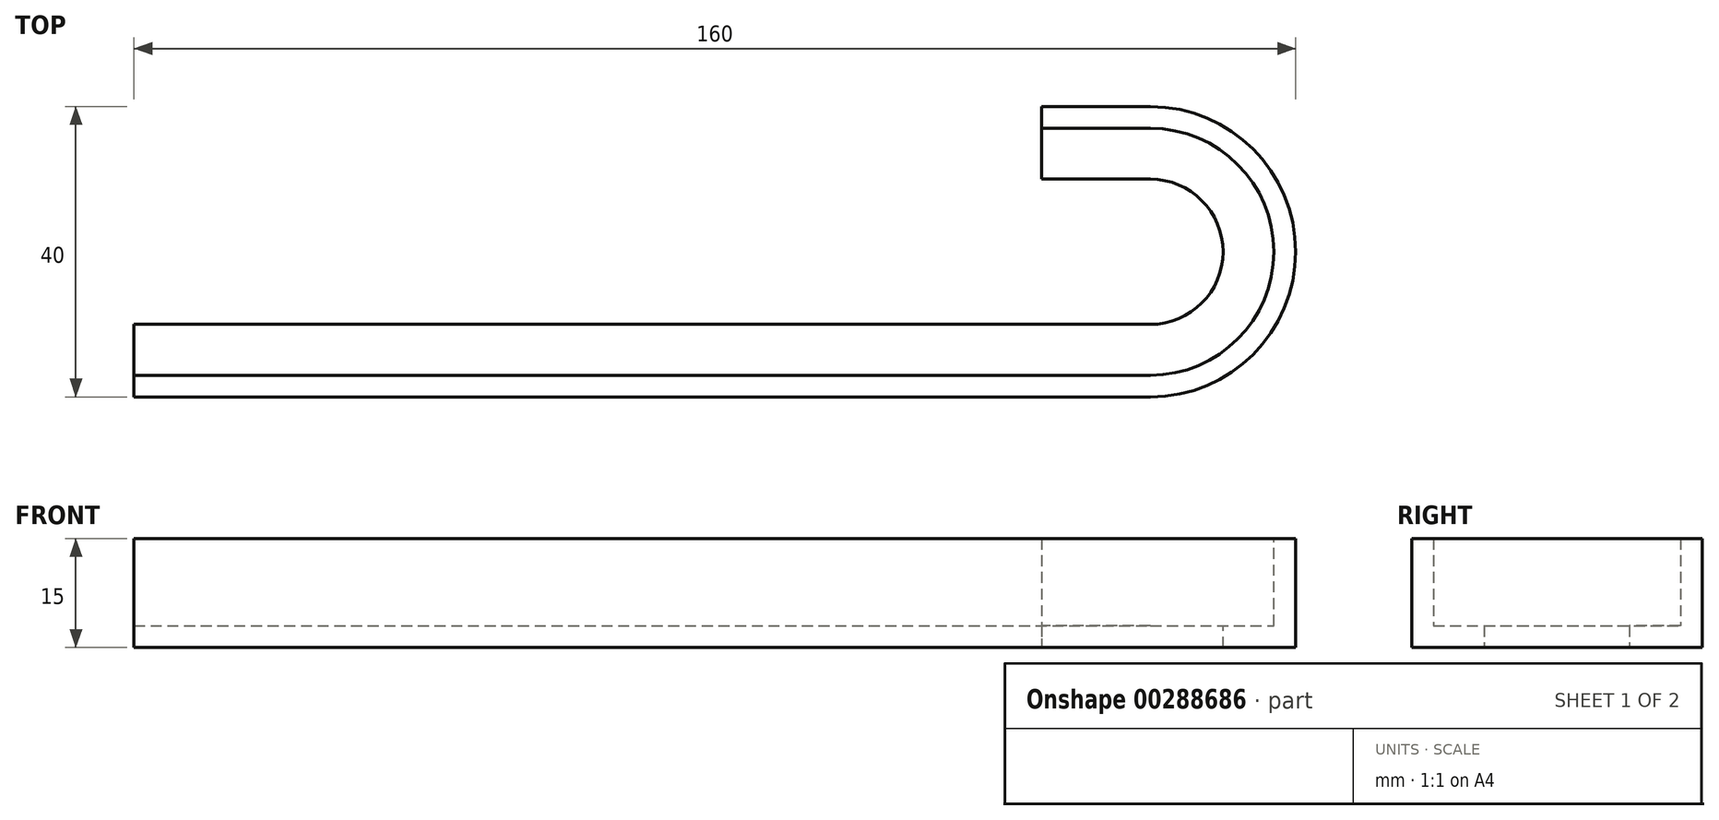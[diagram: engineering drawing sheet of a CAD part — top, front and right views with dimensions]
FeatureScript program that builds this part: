
annotation { "Feature Type Name" : "Feature", "Feature Type Description" : "" }
export const myFeature = defineFeature(function(context is Context, id is Id, definition is map)
    precondition{}
    {
        {
            var Q0;
            Q0=qCreatedBy(makeId("Top.planeOp"),FACE);
            var sketch = newSketch(context, id + "F0", { "sketchPlane" : qUnion([Q0])});
            skLineSegment(sketch, "E0", {"start": v(0, 0) * mm, "end": v(140, 0) * mm});
            skArc(sketch, "E1", {"start": v(140, 0) * mm, "mid": v(160, 20) * mm, "end": v(140, 40) * mm});
            skPoint(sketch, "E2", {"position": v(140, 0) * mm});
            skPoint(sketch, "E3", {"position": v(140, 40) * mm});
            skLineSegment(sketch, "E4", {"start": v(140, 40) * mm, "end": v(125, 40) * mm});
            skSolve(sketch);
        }
        {
            var Q0;
            Q0=qCreatedBy(makeId("Right.planeOp"),FACE);
            var sketch = newSketch(context, id + "F1", { "sketchPlane" : qUnion([Q0])});
            skLineSegment(sketch, "E5", {"start": v(0, 0) * mm, "end": v(10, 0) * mm});
            skLineSegment(sketch, "E6", {"start": v(0, 15) * mm, "end": v(0, 0) * mm});
            skLineSegment(sketch, "E7", {"start": v(0, 15) * mm, "end": v(3, 15) * mm});
            skLineSegment(sketch, "E8", {"start": v(3, 15) * mm, "end": v(3, 3) * mm});
            skLineSegment(sketch, "E9", {"start": v(3, 3) * mm, "end": v(10, 3) * mm});
            skLineSegment(sketch, "E10", {"start": v(10, 3) * mm, "end": v(10, 0) * mm});
            skSolve(sketch);
        }
        {
            var Q0;
            Q0=makeQuery(id+"F1.imprint","IMPRINT",FACE,{"disambiguationData":[TD([[makeQuery(id+"F1.imprint","IMPRINT",EDGE,{"derivedFrom":sQuery(id+"F1.wireOp",EDGE,"E5")}),1.0]])]});
            var Q1;
            Q1=sQuery(id+"F0.wireOp",EDGE,"E0");
            var Q2;
            Q2=sQuery(id+"F0.wireOp",EDGE,"E1");
            var Q3;
            Q3=sQuery(id+"F0.wireOp",EDGE,"E4");
            sweep(context, id + "F2", {"profiles" : qUnion([Q0]), "path" : qUnion([Q1, Q2, Q3])});
        }
    });
